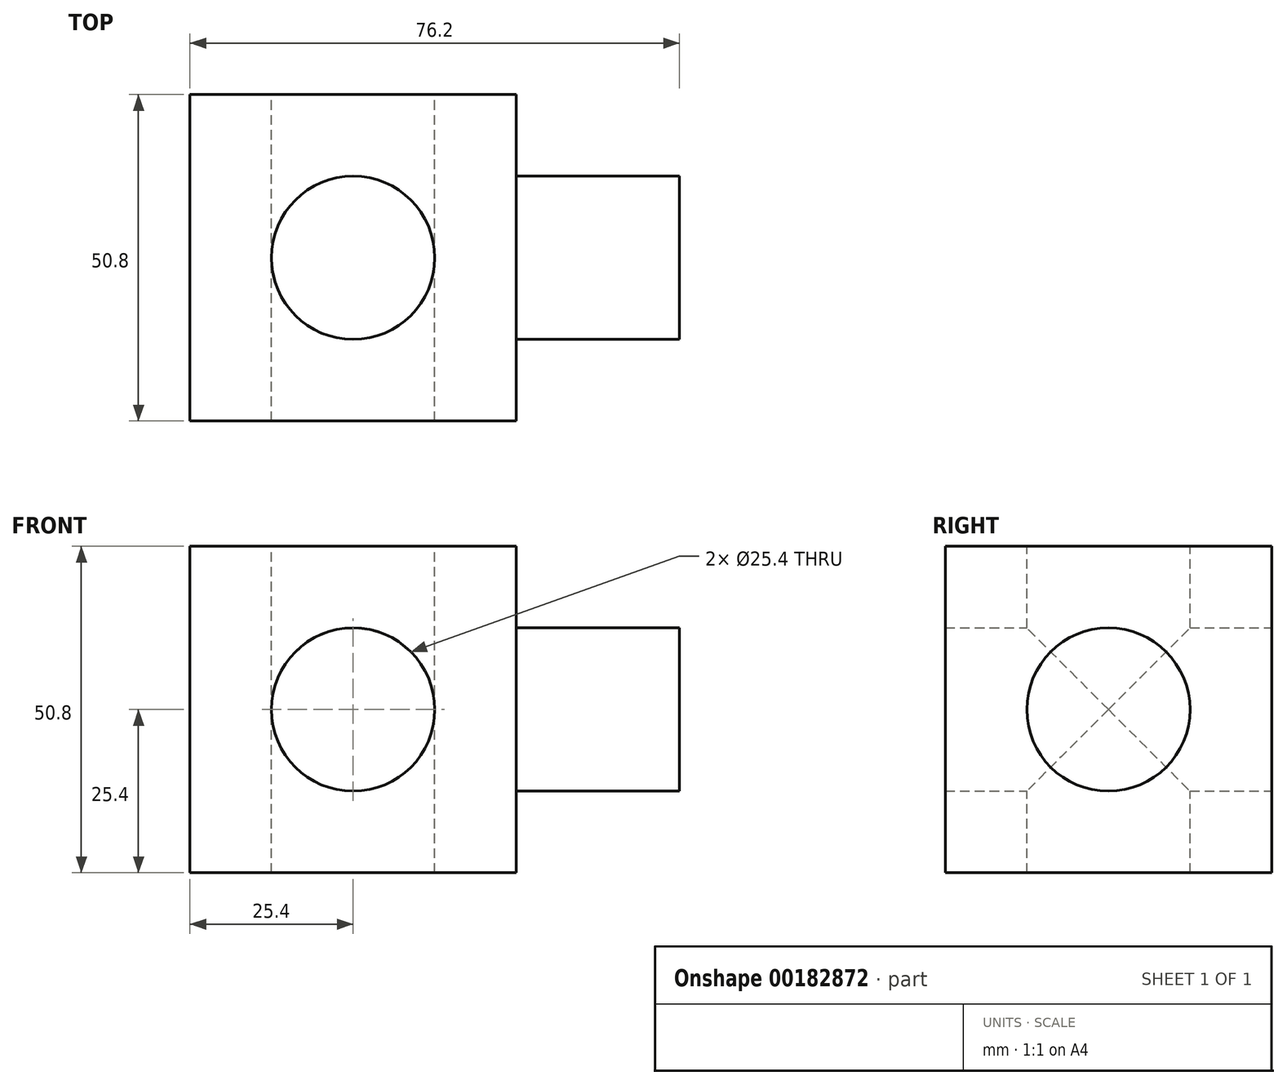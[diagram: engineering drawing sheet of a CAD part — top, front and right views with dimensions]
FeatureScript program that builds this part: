
annotation { "Feature Type Name" : "Feature", "Feature Type Description" : "" }
export const myFeature = defineFeature(function(context is Context, id is Id, definition is map)
    precondition{}
    {
        {
            var Q0;
            Q0=qCreatedBy(makeId("Top.planeOp"),FACE);
            var sketch = newSketch(context, id + "F0", { "sketchPlane" : qUnion([Q0])});
            skLineSegment(sketch, "E0.bottom", {"start": v(25.4, -25.4) * mm, "end": v(-25.4, -25.4) * mm});
            skLineSegment(sketch, "E0.top", {"start": v(25.4, 25.4) * mm, "end": v(-25.4, 25.4) * mm});
            skLineSegment(sketch, "E0.left", {"start": v(25.4, -25.4) * mm, "end": v(25.4, 25.4) * mm});
            skLineSegment(sketch, "E0.right", {"start": v(-25.4, -25.4) * mm, "end": v(-25.4, 25.4) * mm});
            skPoint(sketch, "E0.middle", {"position": v(0, 0) * mm});
            skCircle(sketch, "E1", {"center": v(0, 0) * mm, "radius": 12.7 * mm});
            skSolve(sketch);
        }
        {
            var Q0;
            Q0=qCreatedBy(makeId("Front.planeOp"),FACE);
            var sketch = newSketch(context, id + "F1", { "sketchPlane" : qUnion([Q0])});
            skLineSegment(sketch, "E2", {"start": v(0, 0) * mm, "end": v(0, 50.8) * mm});
            skSolve(sketch);
        }
        {
            var Q0;
            Q0 = qSketchRegion(id + "F0", true);
            var Q1;
            Q1 = qConstructionFilter(qBodyType(qCreatedBy(id + "F1" ,EDGE), BodyType.WIRE), ConstructionObject.NO);
            sweep(context, id + "F2", {"profiles" : qUnion([Q0]), "path" : qUnion([Q1])});
        }
        {
            var Q0;
            Q0=makeQuery(id+"F2.opSweep","SWEPT_FACE",FACE,{"disambiguationData":[OSD([sQuery(id+"F0.wireOp",EDGE,"E0.left"),sQuery(id+"F1.wireOp",EDGE,"E2")])]});
            var sketch = newSketch(context, id + "F3", { "sketchPlane" : qUnion([Q0])});
            skCircle(sketch, "E3", {"center": v(0, 25.4) * mm, "radius": 12.7 * mm});
            skPoint(sketch, "E3.centerSnap0", {"position": v(25.4, 25.4) * mm});
            skSolve(sketch);
        }
        {
            var Q0;
            Q0 = qSketchRegion(id + "F3", true);
            extrude(context, id + "F4", {"entities" : qUnion([Q0]), "operationType" : NewBodyOperationType.ADD, "depth" : 25.4 * mm});
        }
        {
            var Q0;
            Q0=makeQuery(id+"F2.opSweep","SWEPT_FACE",FACE,{"disambiguationData":[OSD([sQuery(id+"F0.wireOp",EDGE,"E0.top"),sQuery(id+"F1.wireOp",EDGE,"E2")])]});
            var sketch = newSketch(context, id + "F5", { "sketchPlane" : qUnion([Q0])});
            skPoint(sketch, "E4", {"position": v(0, 25.4) * mm});
            skPoint(sketch, "E4.positionSnap0", {"position": v(-25.4, 25.4) * mm});
            skSolve(sketch);
        }
        {
            var Q0;
            Q0=sQuery(id+"F5.wireOp",VERTEX,"E4");
            var Q1;
            Q1=makeQuery(id+"F2.opSweep","SWEPT_BODY",BODY,{"disambiguationData":[OSD([sQuery(id+"F0.wireOp",EDGE,"E0.bottom"),sQuery(id+"F0.wireOp",EDGE,"E0.top"),sQuery(id+"F0.wireOp",EDGE,"E0.left"),sQuery(id+"F0.wireOp",EDGE,"E0.right"),sQuery(id+"F0.wireOp",EDGE,"E1"),sQuery(id+"F1.wireOp",EDGE,"E2")])]});
            hole(context, id + "F6", {"style" : HoleStyle.SIMPLE, "endStyle" : HoleEndStyle.THROUGH, "holeDiameter" : 25.4 * mm, "locations" : qUnion([Q0]), "scope" : qUnion([Q1]), "isTappedThrough" : true});
        }
    });
